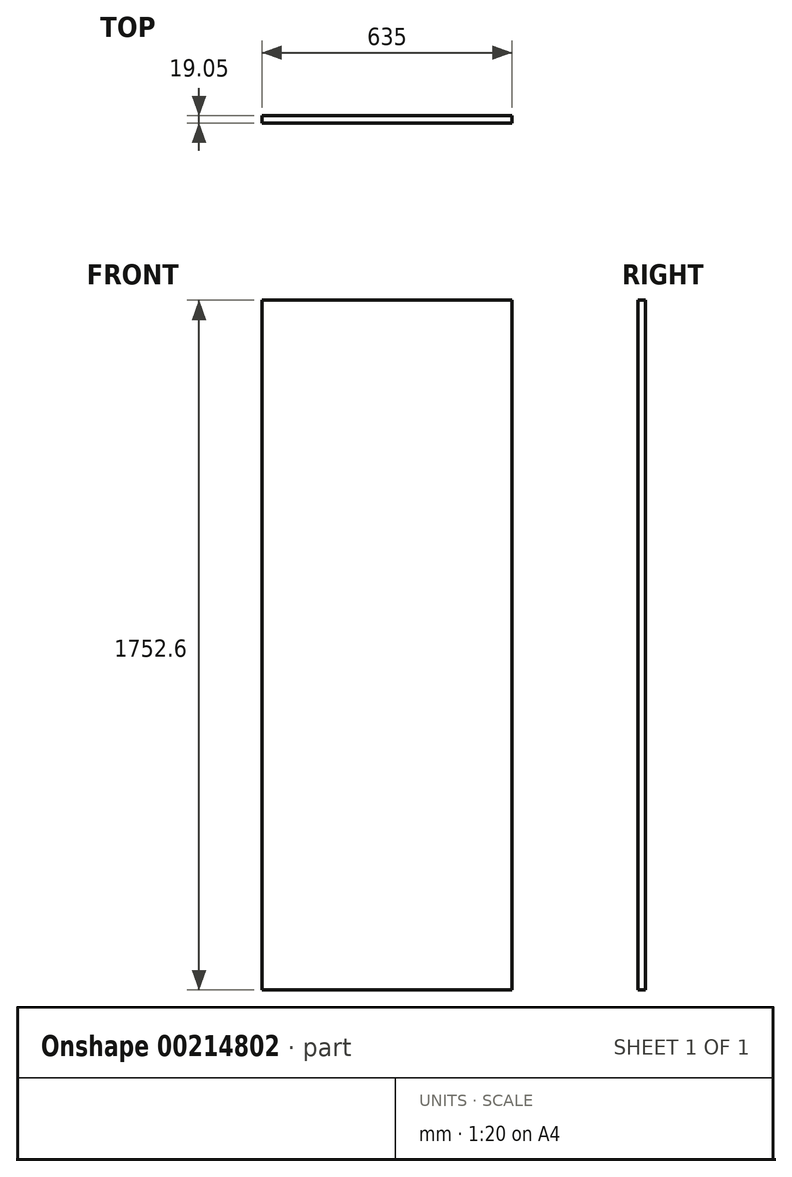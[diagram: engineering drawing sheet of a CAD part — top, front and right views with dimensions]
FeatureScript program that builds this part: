
annotation { "Feature Type Name" : "Feature", "Feature Type Description" : "" }
export const myFeature = defineFeature(function(context is Context, id is Id, definition is map)
    precondition{}
    {
        {
            var Q0;
            Q0=qCreatedBy(makeId("Front.planeOp"),FACE);
            var sketch = newSketch(context, id + "F0", { "sketchPlane" : qUnion([Q0])});
            skLineSegment(sketch, "E0.bottom", {"start": v(0, 0) * mm, "end": v(635, 0) * mm});
            skLineSegment(sketch, "E0.top", {"start": v(0, -1752.6) * mm, "end": v(635, -1752.6) * mm});
            skLineSegment(sketch, "E0.left", {"start": v(0, 0) * mm, "end": v(0, -1752.6) * mm});
            skLineSegment(sketch, "E0.right", {"start": v(635, 0) * mm, "end": v(635, -1752.6) * mm});
            skSolve(sketch);
        }
        {
            var Q0;
            Q0=makeQuery(id+"F0.imprint","IMPRINT",FACE,{"disambiguationData":[TD([[makeQuery(id+"F0.imprint","IMPRINT",EDGE,{"derivedFrom":sQuery(id+"F0.wireOp",EDGE,"E0.bottom")}),-1.0]])]});
            extrude(context, id + "F1", {"entities" : qUnion([Q0]), "depth" : 19.05 * mm});
        }
    });
